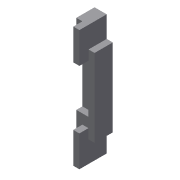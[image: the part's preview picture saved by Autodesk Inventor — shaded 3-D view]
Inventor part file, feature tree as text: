
AUTODESK INVENTOR PART (.ipt)
format: ipt  version: 2016 (Build 200138000, 138)  size: 102,912 bytes
history: native  units: mm
features: extrude x3, sketch x3
ambient origin geometry x8: Origin, YZ Plane, XZ Plane, XY Plane, X Axis, Y Axis, Z Axis, Center Point
bodies: Solid1 (feature_tree)
feature tree (6):
  extrude  "Extrusion1"  Depth=20.0mm
  extrude  "Extrusion6"  Depth=20.0mm
  extrude  "Extrusion7"  Depth=20.0mm
  sketch  "Sketch1"  dims[d16=35.0mm d17=20.0mm]
  sketch  "Sketch2"  dims[d18=35.0mm d19=20.0mm]
  sketch  "Sketch6"  dims[d20=30.0mm d21=0.0mm d22=20.0mm d23=80.0mm d25=24.0mm d28=128.0mm d35=10.0mm d44=10.0mm d45=0.0mm d46=30.0mm d47=0.0mm]
